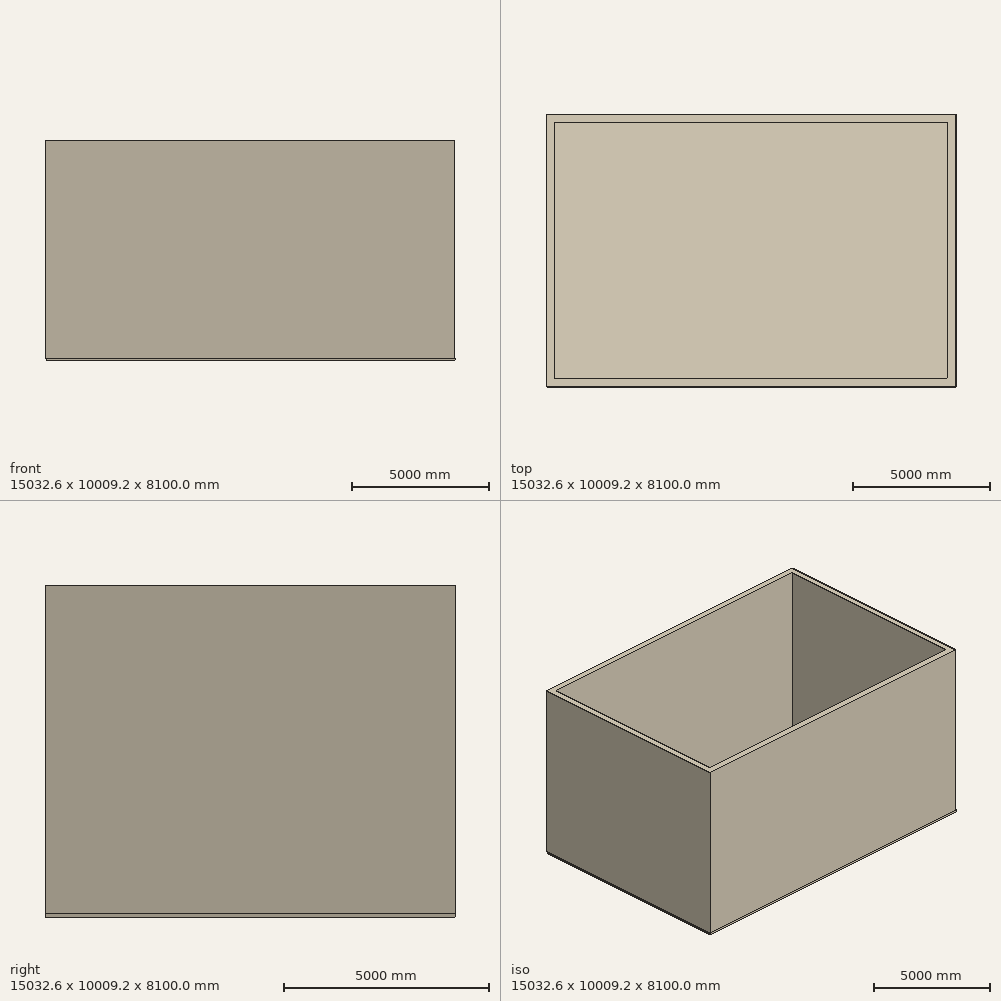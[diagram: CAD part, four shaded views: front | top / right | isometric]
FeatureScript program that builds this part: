
annotation { "Feature Type Name" : "Feature", "Feature Type Description" : "" }
export const myFeature = defineFeature(function(context is Context, id is Id, definition is map)
    precondition{}
    {
        {
            var Q0;
            Q0=qCreatedBy(makeId("Top.planeOp"),FACE);
            var sketch = newSketch(context, id + "F0", { "sketchPlane" : qUnion([Q0])});
            skLineSegment(sketch, "E0.bottom", {"start": v(-7500, -5000) * mm, "end": v(7500, -5000) * mm});
            skLineSegment(sketch, "E0.top", {"start": v(-7500, 5000) * mm, "end": v(7500, 5000) * mm});
            skLineSegment(sketch, "E0.left", {"start": v(-7500, -5000) * mm, "end": v(-7500, 5000) * mm});
            skLineSegment(sketch, "E0.right", {"start": v(7500, -5000) * mm, "end": v(7500, 5000) * mm});
            skPoint(sketch, "E0.middle", {"position": v(0, 0) * mm});
            skSolve(sketch);
        }
        {
            var Q0;
            Q0=makeQuery(id+"F0.imprint","IMPRINT",FACE,{"disambiguationData":[TD([[makeQuery(id+"F0.imprint","IMPRINT",EDGE,{"derivedFrom":sQuery(id+"F0.wireOp",EDGE,"E0.bottom")}),1.0]])]});
            extrude(context, id + "F1", {"entities" : qUnion([Q0]), "oppositeDirection" : true, "depth" : 100 * mm, "offsetDistance" : 25 * mm});
        }
        {
            var Q0;
            Q0=qCreatedBy(makeId("Top.planeOp"),FACE);
            var sketch = newSketch(context, id + "F2", { "sketchPlane" : qUnion([Q0])});
            skLineSegment(sketch, "E1", {"start": v(-7532.6, -4990.75) * mm, "end": v(7467.4, -4990.75) * mm});
            skLineSegment(sketch, "E2", {"start": v(7467.4, -4990.75) * mm, "end": v(7467.4, 5009.25) * mm});
            skLineSegment(sketch, "E3", {"start": v(7467.4, 5009.25) * mm, "end": v(-7532.6, 5009.25) * mm});
            skLineSegment(sketch, "E4", {"start": v(-7532.6, 5009.25) * mm, "end": v(-7532.6, -4990.75) * mm});
            skLineSegment(sketch, "E5.0", {"start": v(-7232.6, 4709.25) * mm, "end": v(-7232.6, -4690.75) * mm});
            skLineSegment(sketch, "E5.1", {"start": v(7167.4, 4709.25) * mm, "end": v(-7232.6, 4709.25) * mm});
            skLineSegment(sketch, "E5.2", {"start": v(7167.4, -4690.75) * mm, "end": v(7167.4, 4709.25) * mm});
            skLineSegment(sketch, "E5.3", {"start": v(-7232.6, -4690.75) * mm, "end": v(7167.4, -4690.75) * mm});
            skSolve(sketch);
        }
        {
            var Q0;
            Q0=makeQuery(id+"F2.imprint","IMPRINT",FACE,{"disambiguationData":[TD([[makeQuery(id+"F2.imprint","IMPRINT",EDGE,{"derivedFrom":sQuery(id+"F2.wireOp",EDGE,"E1")}),1.0]])]});
            extrude(context, id + "F3", {"entities" : qUnion([Q0]), "operationType" : NewBodyOperationType.ADD, "depth" : 8000 * mm, "offsetDistance" : 25 * mm});
        }
    });
